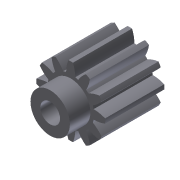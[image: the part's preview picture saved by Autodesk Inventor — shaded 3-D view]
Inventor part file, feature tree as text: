
AUTODESK INVENTOR PART (.ipt)
format: ipt  version: 2011 (Build 150239000, 239)  size: 195,072 bytes
history: native  units: mm (DEFAULTED — no unit token found)
features: other x4, sketch x4, extrude x3, plane x3
ambient origin geometry x8: Origin, YZ Plane, XZ Plane, XY Plane, X Axis, Y Axis, Z Axis, Center Point
bodies: Solid1 (feature_tree)
feature tree (14):
  other  "Gear 12T 32dp 125press"
  extrude  "Extrusion1"  Depth=9.525mm TaperAngle=0.0deg
  plane  "Work Plane1"
  plane  "Work Plane2"
  plane  "Work Plane3"
  other  "Spur Gear"
  extrude  "Extrusion2"  Depth=76.2mm TaperAngle=0.0deg
  extrude  "Extrusion3"  TaperAngle=0.0deg  [1 undecoded]
  sketch  "Sketch1"  dims[d0=11.1125mm d1=9.525mm d2=0.0mm]
  sketch  "Sketch2"  dims[d3=9.525mm d4=76.2mm d5=0.0mm]
  other  "Srf1"
  sketch  "Sketch3"  dims[d6=0.0mm d7=15.0deg d9=0.0mm]
  sketch  "Sketch4"  dims[d14=0.0mm d15=9.525mm d16=0.0mm d17=0.0mm d18=0.0mm d19=9.525mm d20=3.175mm d21=6.35mm d22=3.302mm d23=0.0mm d24=3.175mm d25=3.302mm d26=0.0mm]
  other  "Pitch Diameter"
note: 1 required parameter value undecoded (feature->parameter linkage not recoverable at this tier; creation-order binding heuristic only, values carry confidence <= 0.55)
